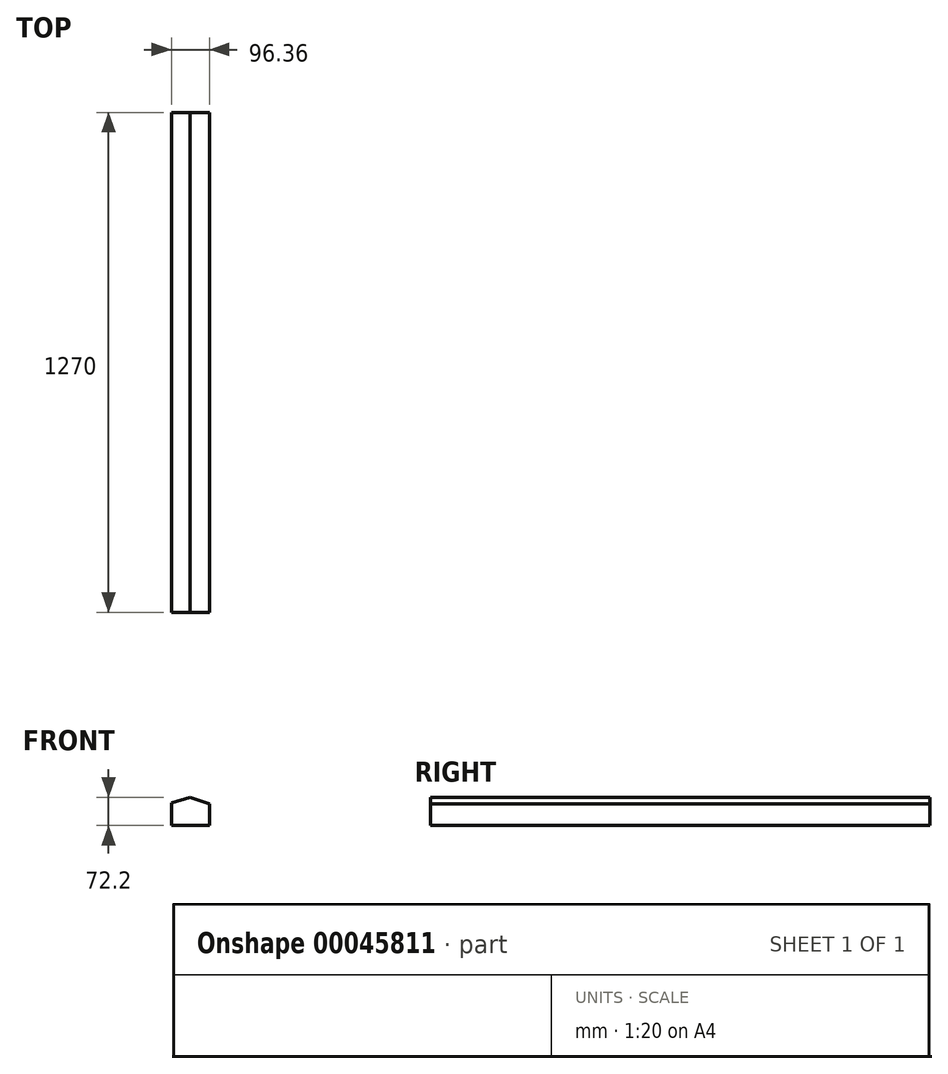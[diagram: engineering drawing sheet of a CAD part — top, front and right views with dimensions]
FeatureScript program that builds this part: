
annotation { "Feature Type Name" : "Feature", "Feature Type Description" : "" }
export const myFeature = defineFeature(function(context is Context, id is Id, definition is map)
    precondition{}
    {
        {
            var Q0;
            Q0=qCreatedBy(makeId("Front.planeOp"),FACE);
            var sketch = newSketch(context, id + "F0", { "sketchPlane" : qUnion([Q0])});
            skLineSegment(sketch, "E0", {"start": v(0, 0) * mm, "end": v(0, 57.53) * mm});
            skLineSegment(sketch, "E1", {"start": v(0, 57.53) * mm, "end": v(46.84, 72.2) * mm});
            skLineSegment(sketch, "E2", {"start": v(46.84, 72.2) * mm, "end": v(96.36, 54.98) * mm});
            skLineSegment(sketch, "E3", {"start": v(96.36, 54.98) * mm, "end": v(96.36, 0) * mm});
            skLineSegment(sketch, "E4", {"start": v(96.36, 0) * mm, "end": v(0, 0) * mm});
            skSolve(sketch);
        }
        {
            var Q0;
            Q0=makeQuery(id+"F0.imprint","IMPRINT",FACE,{"disambiguationData":[TD([[makeQuery(id+"F0.imprint","IMPRINT",EDGE,{"derivedFrom":sQuery(id+"F0.wireOp",EDGE,"E0")}),-1.0]])]});
            extrude(context, id + "F1", {"entities" : qUnion([Q0]), "depth" : 1270 * mm});
        }
    });
